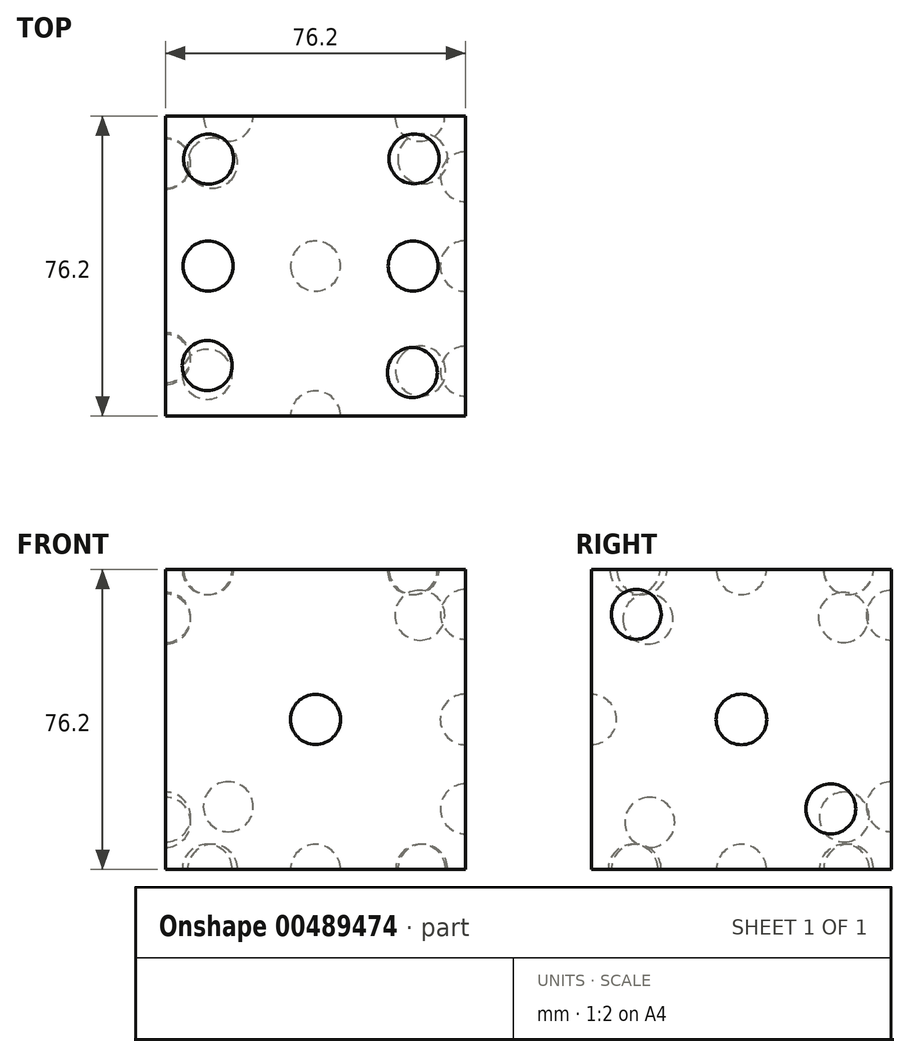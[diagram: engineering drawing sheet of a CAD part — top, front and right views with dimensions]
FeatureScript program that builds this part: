
annotation { "Feature Type Name" : "Feature", "Feature Type Description" : "" }
export const myFeature = defineFeature(function(context is Context, id is Id, definition is map)
    precondition{}
    {
        {
            var Q0;
            Q0=qCreatedBy(makeId("Front.planeOp"),FACE);
            var sketch = newSketch(context, id + "F0", { "sketchPlane" : qUnion([Q0])});
            skLineSegment(sketch, "E0", {"start": v(0, 0) * mm, "end": v(-76.2, 0) * mm});
            skLineSegment(sketch, "E1", {"start": v(0, 76.2) * mm, "end": v(-76.2, 76.2) * mm});
            skLineSegment(sketch, "E2", {"start": v(-76.2, 76.2) * mm, "end": v(-76.2, 0) * mm});
            skLineSegment(sketch, "E3", {"start": v(0, 76.2) * mm, "end": v(0, 0) * mm});
            skSolve(sketch);
        }
        {
            var Q0;
            Q0 = qSketchRegion(id + "F0", true);
            extrude(context, id + "F1", {"entities" : qUnion([Q0]), "depth" : 76.2 * mm});
        }
        {
            var Q0;
            Q0=makeQuery(id+"F1.opExtrude","CAP_FACE",FACE,{"disambiguationData":[OSD([sQuery(id+"F0.wireOp",EDGE,"E0"),sQuery(id+"F0.wireOp",EDGE,"E1"),sQuery(id+"F0.wireOp",EDGE,"E2"),sQuery(id+"F0.wireOp",EDGE,"E3")])],"isStart":false});
            var sketch = newSketch(context, id + "F2", { "sketchPlane" : qUnion([Q0])});
            skLineSegment(sketch, "E4", {"start": v(-38.1, 76.2) * mm, "end": v(-38.1, 0) * mm});
            skPoint(sketch, "E5.endSnap0", {"position": v(-76.2, 38.1) * mm});
            skPoint(sketch, "E6.end.orphan", {"position": v(0, 38.1) * mm});
            skPoint(sketch, "E7.orphan", {"position": v(-4, 38.1) * mm});
            skPoint(sketch, "E5.start.orphan", {"position": v(-76.2, 38.1) * mm});
            skArc(sketch, "E8", {"start": v(-38.1, 31.75) * mm, "mid": v(-31.75, 38.1) * mm, "end": v(-38.1, 44.45) * mm});
            skSolve(sketch);
        }
        {
            var Q0;
            Q0 = qSketchRegion(id + "F2", true);
            var Q1;
            Q1=sQuery(id+"F2.wireOp",EDGE,"E4");
            revolve(context, id + "F3", {"operationType" : NewBodyOperationType.REMOVE, "entities" : qUnion([Q0]), "axis" : qUnion([Q1]), "revolveType" : RevolveType.FULL, "oppositeDirection" : true});
        }
        {
            var Q0;
            Q0=makeQuery(id+"F1.opExtrude","CAP_FACE",FACE,{"disambiguationData":[OSD([sQuery(id+"F0.wireOp",EDGE,"E0"),sQuery(id+"F0.wireOp",EDGE,"E1"),sQuery(id+"F0.wireOp",EDGE,"E2"),sQuery(id+"F0.wireOp",EDGE,"E3")])],"isStart":true});
            var sketch = newSketch(context, id + "F4", { "sketchPlane" : qUnion([Q0])});
            skArc(sketch, "E9", {"start": v(11.38, 58.24) * mm, "mid": v(17.96, 64.61) * mm, "end": v(11.33, 70.93) * mm});
            skPoint(sketch, "E10.orphan", {"position": v(11.61, 0) * mm});
            skPoint(sketch, "E11.end.orphan", {"position": v(11.61, 76.2) * mm});
            skPoint(sketch, "E12.orphan", {"position": v(59.49, 0) * mm});
            skPoint(sketch, "E13.orphan", {"position": v(59.49, 76.2) * mm});
            skLineSegment(sketch, "E14", {"start": v(11.61, 76.2) * mm, "end": v(11.61, 0) * mm});
            skSolve(sketch);
        }
        {
            var Q0;
            Q0 = qSketchRegion(id + "F4", true);
            var Q1;
            Q1=sQuery(id+"F4.wireOp",EDGE,"E14");
            revolve(context, id + "F5", {"operationType" : NewBodyOperationType.REMOVE, "entities" : qUnion([Q0]), "axis" : qUnion([Q1]), "revolveType" : RevolveType.FULL, "oppositeDirection" : true});
        }
        {
            var Q0;
            Q0=makeQuery(id+"F1.opExtrude","CAP_FACE",FACE,{"disambiguationData":[OSD([sQuery(id+"F0.wireOp",EDGE,"E0"),sQuery(id+"F0.wireOp",EDGE,"E1"),sQuery(id+"F0.wireOp",EDGE,"E2"),sQuery(id+"F0.wireOp",EDGE,"E3")])],"isStart":true});
            var sketch = newSketch(context, id + "F6", { "sketchPlane" : qUnion([Q0])});
            skArc(sketch, "E15", {"start": v(60.26, 9.59) * mm, "mid": v(66.61, 15.94) * mm, "end": v(60.26, 22.29) * mm});
            skLineSegment(sketch, "E16", {"start": v(60.26, 76.2) * mm, "end": v(60.26, 0) * mm});
            skSolve(sketch);
        }
        {
            var Q0;
            Q0 = qSketchRegion(id + "F6", true);
            var Q1;
            Q1=sQuery(id+"F6.wireOp",EDGE,"E16");
            revolve(context, id + "F7", {"operationType" : NewBodyOperationType.REMOVE, "entities" : qUnion([Q0]), "axis" : qUnion([Q1]), "revolveType" : RevolveType.FULL, "oppositeDirection" : true});
        }
        {
            var Q0;
            Q0=makeQuery(id+"F1.opExtrude","SWEPT_FACE",FACE,{"disambiguationData":[OSD([sQuery(id+"F0.wireOp",EDGE,"E3")])]});
            var sketch = newSketch(context, id + "F8", { "sketchPlane" : qUnion([Q0])});
            skArc(sketch, "E17", {"start": v(-64.83, 58.48) * mm, "mid": v(-58.48, 64.83) * mm, "end": v(-64.83, 71.18) * mm});
            skPoint(sketch, "E18.orphan", {"position": v(-76.2, 76.2) * mm});
            skPoint(sketch, "E19.trimOffspring.end.orphan", {"position": v(0, 0) * mm});
            skLineSegment(sketch, "E20", {"start": v(-64.83, 76.2) * mm, "end": v(-64.83, 0) * mm});
            skPoint(sketch, "E21.orphan", {"position": v(-38.1, 76.2) * mm});
            skPoint(sketch, "E22.center.orphan", {"position": v(-38.1, 38.1) * mm});
            skPoint(sketch, "E23.end.orphan", {"position": v(-38.1, 0) * mm});
            skPoint(sketch, "E24.orphan", {"position": v(-12.52, 76.2) * mm});
            skPoint(sketch, "E25.center.orphan", {"position": v(-12.52, 12.52) * mm});
            skSolve(sketch);
        }
        {
            var Q0;
            Q0 = qSketchRegion(id + "F8", true);
            var Q1;
            Q1=sQuery(id+"F8.wireOp",EDGE,"E20");
            revolve(context, id + "F9", {"operationType" : NewBodyOperationType.REMOVE, "entities" : qUnion([Q0]), "axis" : qUnion([Q1]), "revolveType" : RevolveType.FULL, "oppositeDirection" : true});
        }
        {
            var Q0;
            Q0=makeQuery(id+"F1.opExtrude","SWEPT_FACE",FACE,{"disambiguationData":[OSD([sQuery(id+"F0.wireOp",EDGE,"E3")])]});
            var sketch = newSketch(context, id + "F10", { "sketchPlane" : qUnion([Q0])});
            skArc(sketch, "E26", {"start": v(-38.1, 31.67) * mm, "mid": v(-31.67, 38.1) * mm, "end": v(-38.1, 44.53) * mm});
            skPoint(sketch, "E27.orphan", {"position": v(-76.2, 76.2) * mm});
            skPoint(sketch, "E28.orphan", {"position": v(0, 0) * mm});
            skLineSegment(sketch, "E29", {"start": v(-38.1, 76.2) * mm, "end": v(-38.1, 0) * mm});
            skSolve(sketch);
        }
        {
            var Q0;
            Q0 = qSketchRegion(id + "F10", true);
            var Q1;
            Q1=sQuery(id+"F10.wireOp",EDGE,"E29");
            revolve(context, id + "F11", {"operationType" : NewBodyOperationType.REMOVE, "entities" : qUnion([Q0]), "axis" : qUnion([Q1]), "revolveType" : RevolveType.FULL, "oppositeDirection" : true});
        }
        {
            var Q0;
            Q0=makeQuery(id+"F1.opExtrude","SWEPT_FACE",FACE,{"disambiguationData":[OSD([sQuery(id+"F0.wireOp",EDGE,"E3")])]});
            var sketch = newSketch(context, id + "F12", { "sketchPlane" : qUnion([Q0])});
            skArc(sketch, "E30", {"start": v(-15.4, 9.05) * mm, "mid": v(-9.05, 15.4) * mm, "end": v(-15.4, 21.75) * mm});
            skLineSegment(sketch, "E31", {"start": v(-15.4, 76.2) * mm, "end": v(-15.4, 0) * mm});
            skSolve(sketch);
        }
        {
            var Q0;
            Q0 = qSketchRegion(id + "F12", true);
            var Q1;
            Q1=sQuery(id+"F12.wireOp",EDGE,"E31");
            revolve(context, id + "F13", {"operationType" : NewBodyOperationType.REMOVE, "entities" : qUnion([Q0]), "axis" : qUnion([Q1]), "revolveType" : RevolveType.FULL, "oppositeDirection" : true});
        }
        {
            var Q0;
            Q0=makeQuery(id+"F1.opExtrude","SWEPT_FACE",FACE,{"disambiguationData":[OSD([sQuery(id+"F0.wireOp",EDGE,"E2")])]});
            var sketch = newSketch(context, id + "F14", { "sketchPlane" : qUnion([Q0])});
            skArc(sketch, "E32", {"start": v(12.17, 57.68) * mm, "mid": v(18.52, 64.03) * mm, "end": v(12.17, 70.38) * mm});
            skLineSegment(sketch, "E33", {"start": v(12.17, 76.2) * mm, "end": v(12.17, 0) * mm});
            skSolve(sketch);
        }
        {
            var Q0;
            Q0 = qSketchRegion(id + "F14", true);
            var Q1;
            Q1=sQuery(id+"F14.wireOp",EDGE,"E33");
            revolve(context, id + "F15", {"operationType" : NewBodyOperationType.REMOVE, "entities" : qUnion([Q0]), "axis" : qUnion([Q1]), "revolveType" : RevolveType.FULL, "oppositeDirection" : true});
        }
        {
            var Q0;
            Q0=makeQuery(id+"F1.opExtrude","SWEPT_FACE",FACE,{"disambiguationData":[OSD([sQuery(id+"F0.wireOp",EDGE,"E2")])]});
            var sketch = newSketch(context, id + "F16", { "sketchPlane" : qUnion([Q0])});
            skLineSegment(sketch, "E34", {"start": v(11.97, 76.2) * mm, "end": v(11.97, 0) * mm});
            skArc(sketch, "E35", {"start": v(11.97, 6.95) * mm, "mid": v(18.32, 13.3) * mm, "end": v(11.97, 19.65) * mm});
            skSolve(sketch);
        }
        {
            var Q0;
            Q0 = qSketchRegion(id + "F16", true);
            var Q1;
            Q1=sQuery(id+"F16.wireOp",EDGE,"E34");
            revolve(context, id + "F17", {"operationType" : NewBodyOperationType.REMOVE, "entities" : qUnion([Q0]), "axis" : qUnion([Q1]), "revolveType" : RevolveType.FULL, "oppositeDirection" : true});
        }
        {
            var Q0;
            Q0=makeQuery(id+"F1.opExtrude","SWEPT_FACE",FACE,{"disambiguationData":[OSD([sQuery(id+"F0.wireOp",EDGE,"E2")])]});
            var sketch = newSketch(context, id + "F18", { "sketchPlane" : qUnion([Q0])});
            skLineSegment(sketch, "E36", {"start": v(0, 63.6) * mm, "end": v(76.2, 63.6) * mm});
            skArc(sketch, "E37", {"start": v(68.19, 63.6) * mm, "mid": v(61.84, 69.96) * mm, "end": v(55.49, 63.6) * mm});
            skSolve(sketch);
        }
        {
            var Q0;
            Q0 = qSketchRegion(id + "F18", true);
            var Q1;
            Q1=sQuery(id+"F18.wireOp",EDGE,"E36");
            revolve(context, id + "F19", {"operationType" : NewBodyOperationType.REMOVE, "entities" : qUnion([Q0]), "axis" : qUnion([Q1]), "revolveType" : RevolveType.FULL, "oppositeDirection" : true});
        }
        {
            var Q0;
            Q0=makeQuery(id+"F1.opExtrude","SWEPT_FACE",FACE,{"disambiguationData":[OSD([sQuery(id+"F0.wireOp",EDGE,"E2")])]});
            var sketch = newSketch(context, id + "F20", { "sketchPlane" : qUnion([Q0])});
            skLineSegment(sketch, "E38", {"start": v(61.4, 76.2) * mm, "end": v(61.4, 0) * mm});
            skArc(sketch, "E39", {"start": v(61.4, 5.62) * mm, "mid": v(67.74, 11.97) * mm, "end": v(61.4, 18.32) * mm});
            skSolve(sketch);
        }
        {
            var Q0;
            Q0 = qSketchRegion(id + "F20", true);
            var Q1;
            Q1=sQuery(id+"F20.wireOp",EDGE,"E38");
            revolve(context, id + "F21", {"operationType" : NewBodyOperationType.REMOVE, "entities" : qUnion([Q0]), "axis" : qUnion([Q1]), "revolveType" : RevolveType.FULL, "oppositeDirection" : true});
        }
        {
            var Q0;
            Q0=makeQuery(id+"F1.opExtrude","SWEPT_FACE",FACE,{"disambiguationData":[OSD([sQuery(id+"F0.wireOp",EDGE,"E0")])]});
            var sketch = newSketch(context, id + "F22", { "sketchPlane" : qUnion([Q0])});
            skLineSegment(sketch, "E40", {"start": v(-76.2, 76.2) * mm, "end": v(0, 0) * mm});
            skArc(sketch, "E41", {"start": v(-61.11, 61.11) * mm, "mid": v(-61.11, 70.1) * mm, "end": v(-70.1, 70.1) * mm});
            skSolve(sketch);
        }
        {
            var Q0;
            Q0 = qSketchRegion(id + "F22", true);
            var Q1;
            Q1=sQuery(id+"F22.wireOp",EDGE,"E40");
            revolve(context, id + "F23", {"operationType" : NewBodyOperationType.REMOVE, "entities" : qUnion([Q0]), "axis" : qUnion([Q1]), "revolveType" : RevolveType.FULL, "oppositeDirection" : true});
        }
        {
            var Q0;
            Q0=makeQuery(id+"F1.opExtrude","SWEPT_FACE",FACE,{"disambiguationData":[OSD([sQuery(id+"F0.wireOp",EDGE,"E0")])]});
            var sketch = newSketch(context, id + "F24", { "sketchPlane" : qUnion([Q0])});
            skLineSegment(sketch, "E42", {"start": v(-76.2, 76.2) * mm, "end": v(0, 0) * mm});
            skArc(sketch, "E43", {"start": v(-33.6, 33.6) * mm, "mid": v(-33.6, 42.6) * mm, "end": v(-42.6, 42.6) * mm});
            skSolve(sketch);
        }
        {
            var Q0;
            Q0 = qSketchRegion(id + "F24", true);
            var Q1;
            Q1=sQuery(id+"F24.wireOp",EDGE,"E42");
            revolve(context, id + "F25", {"operationType" : NewBodyOperationType.REMOVE, "entities" : qUnion([Q0]), "axis" : qUnion([Q1]), "revolveType" : RevolveType.FULL, "oppositeDirection" : true});
        }
        {
            var Q0;
            Q0=makeQuery(id+"F1.opExtrude","SWEPT_FACE",FACE,{"disambiguationData":[OSD([sQuery(id+"F0.wireOp",EDGE,"E0")])]});
            var sketch = newSketch(context, id + "F26", { "sketchPlane" : qUnion([Q0])});
            skLineSegment(sketch, "E44", {"start": v(-76.2, 76.2) * mm, "end": v(0, 0) * mm});
            skArc(sketch, "E45", {"start": v(-6.37, 6.37) * mm, "mid": v(-6.37, 15.35) * mm, "end": v(-15.35, 15.35) * mm});
            skSolve(sketch);
        }
        {
            var Q0;
            Q0 = qSketchRegion(id + "F26", true);
            var Q1;
            Q1=sQuery(id+"F26.wireOp",EDGE,"E44");
            revolve(context, id + "F27", {"operationType" : NewBodyOperationType.REMOVE, "entities" : qUnion([Q0]), "axis" : qUnion([Q1]), "revolveType" : RevolveType.FULL, "oppositeDirection" : true});
        }
        {
            var Q0;
            Q0=makeQuery(id+"F1.opExtrude","SWEPT_FACE",FACE,{"disambiguationData":[OSD([sQuery(id+"F0.wireOp",EDGE,"E0")])]});
            var sketch = newSketch(context, id + "F28", { "sketchPlane" : qUnion([Q0])});
            skLineSegment(sketch, "E46", {"start": v(0, 76.2) * mm, "end": v(-76.2, 0) * mm});
            skArc(sketch, "E47", {"start": v(-68.74, 7.46) * mm, "mid": v(-59.76, 7.46) * mm, "end": v(-59.76, 16.44) * mm});
            skSolve(sketch);
        }
        {
            var Q0;
            Q0 = qSketchRegion(id + "F28", true);
            var Q1;
            Q1=sQuery(id+"F28.wireOp",EDGE,"E46");
            revolve(context, id + "F29", {"operationType" : NewBodyOperationType.REMOVE, "entities" : qUnion([Q0]), "axis" : qUnion([Q1]), "revolveType" : RevolveType.FULL, "oppositeDirection" : true});
        }
        {
            var Q0;
            Q0=makeQuery(id+"F1.opExtrude","SWEPT_FACE",FACE,{"disambiguationData":[OSD([sQuery(id+"F0.wireOp",EDGE,"E0")])]});
            var sketch = newSketch(context, id + "F30", { "sketchPlane" : qUnion([Q0])});
            skLineSegment(sketch, "E48", {"start": v(0, 76.2) * mm, "end": v(-76.2, 0) * mm});
            skArc(sketch, "E49", {"start": v(-15.88, 60.32) * mm, "mid": v(-6.9, 60.32) * mm, "end": v(-6.9, 69.3) * mm});
            skSolve(sketch);
        }
        {
            var Q0;
            Q0 = qSketchRegion(id + "F30", true);
            var Q1;
            Q1=sQuery(id+"F30.wireOp",EDGE,"E48");
            revolve(context, id + "F31", {"operationType" : NewBodyOperationType.REMOVE, "entities" : qUnion([Q0]), "axis" : qUnion([Q1]), "revolveType" : RevolveType.FULL, "oppositeDirection" : true});
        }
        {
            var Q0;
            Q0=makeQuery(id+"F1.opExtrude","SWEPT_FACE",FACE,{"disambiguationData":[OSD([sQuery(id+"F0.wireOp",EDGE,"E1")])]});
            var sketch = newSketch(context, id + "F32", { "sketchPlane" : qUnion([Q0])});
            skLineSegment(sketch, "E50", {"start": v(-76.2, 0) * mm, "end": v(0, -76.2) * mm});
            skArc(sketch, "E51", {"start": v(-60.76, -15.44) * mm, "mid": v(-60.76, -6.46) * mm, "end": v(-69.74, -6.46) * mm});
            skSolve(sketch);
        }
        {
            var Q0;
            Q0 = qSketchRegion(id + "F32", true);
            var Q1;
            Q1=sQuery(id+"F32.wireOp",EDGE,"E50");
            revolve(context, id + "F33", {"operationType" : NewBodyOperationType.REMOVE, "entities" : qUnion([Q0]), "axis" : qUnion([Q1]), "revolveType" : RevolveType.FULL, "oppositeDirection" : true});
        }
        {
            var Q0;
            Q0=makeQuery(id+"F1.opExtrude","SWEPT_FACE",FACE,{"disambiguationData":[OSD([sQuery(id+"F0.wireOp",EDGE,"E1")])]});
            var sketch = newSketch(context, id + "F34", { "sketchPlane" : qUnion([Q0])});
            skLineSegment(sketch, "E52", {"start": v(-65.38, 0) * mm, "end": v(-65.38, -76.2) * mm});
            skArc(sketch, "E53", {"start": v(-65.38, -44.45) * mm, "mid": v(-59.03, -38.1) * mm, "end": v(-65.38, -31.75) * mm});
            skSolve(sketch);
        }
        {
            var Q0;
            Q0 = qSketchRegion(id + "F34", true);
            var Q1;
            Q1=sQuery(id+"F34.wireOp",EDGE,"E52");
            revolve(context, id + "F35", {"operationType" : NewBodyOperationType.REMOVE, "entities" : qUnion([Q0]), "axis" : qUnion([Q1]), "revolveType" : RevolveType.FULL, "oppositeDirection" : true});
        }
        {
            var Q0;
            Q0=makeQuery(id+"F1.opExtrude","SWEPT_FACE",FACE,{"disambiguationData":[OSD([sQuery(id+"F0.wireOp",EDGE,"E1")])]});
            var sketch = newSketch(context, id + "F36", { "sketchPlane" : qUnion([Q0])});
            skLineSegment(sketch, "E54", {"start": v(-65.6, -76.2) * mm, "end": v(-65.6, 0) * mm});
            skArc(sketch, "E55", {"start": v(-65.6, -69.74) * mm, "mid": v(-59.25, -63.39) * mm, "end": v(-65.6, -57.04) * mm});
            skSolve(sketch);
        }
        {
            var Q0;
            Q0 = qSketchRegion(id + "F36", true);
            var Q1;
            Q1=sQuery(id+"F36.wireOp",EDGE,"E54");
            revolve(context, id + "F37", {"operationType" : NewBodyOperationType.REMOVE, "entities" : qUnion([Q0]), "axis" : qUnion([Q1]), "revolveType" : RevolveType.FULL, "oppositeDirection" : true});
        }
        {
            var Q0;
            Q0=makeQuery(id+"F1.opExtrude","SWEPT_FACE",FACE,{"disambiguationData":[OSD([sQuery(id+"F0.wireOp",EDGE,"E1")])]});
            var sketch = newSketch(context, id + "F38", { "sketchPlane" : qUnion([Q0])});
            skLineSegment(sketch, "E56", {"start": v(-76.2, -10.86) * mm, "end": v(0, -10.86) * mm});
            skArc(sketch, "E57", {"start": v(-6.73, -10.86) * mm, "mid": v(-13.08, -4.51) * mm, "end": v(-19.43, -10.86) * mm});
            skSolve(sketch);
        }
        {
            var Q0;
            Q0 = qSketchRegion(id + "F38", true);
            var Q1;
            Q1=sQuery(id+"F38.wireOp",EDGE,"E56");
            revolve(context, id + "F39", {"operationType" : NewBodyOperationType.REMOVE, "entities" : qUnion([Q0]), "axis" : qUnion([Q1]), "revolveType" : RevolveType.FULL, "oppositeDirection" : true});
        }
        {
            var Q0;
            Q0=makeQuery(id+"F1.opExtrude","SWEPT_FACE",FACE,{"disambiguationData":[OSD([sQuery(id+"F0.wireOp",EDGE,"E1")])]});
            var sketch = newSketch(context, id + "F40", { "sketchPlane" : qUnion([Q0])});
            skLineSegment(sketch, "E58", {"start": v(-13.3, 0) * mm, "end": v(-13.3, -76.2) * mm});
            skArc(sketch, "E59", {"start": v(-13.3, -44.45) * mm, "mid": v(-6.95, -38.1) * mm, "end": v(-13.3, -31.75) * mm});
            skSolve(sketch);
        }
        {
            var Q0;
            Q0 = qSketchRegion(id + "F40", true);
            var Q1;
            Q1=sQuery(id+"F40.wireOp",EDGE,"E58");
            revolve(context, id + "F41", {"operationType" : NewBodyOperationType.REMOVE, "entities" : qUnion([Q0]), "axis" : qUnion([Q1]), "revolveType" : RevolveType.FULL, "oppositeDirection" : true});
        }
        {
            var Q0;
            Q0=makeQuery(id+"F1.opExtrude","SWEPT_FACE",FACE,{"disambiguationData":[OSD([sQuery(id+"F0.wireOp",EDGE,"E1")])]});
            var sketch = newSketch(context, id + "F42", { "sketchPlane" : qUnion([Q0])});
            skLineSegment(sketch, "E60", {"start": v(-13.52, 0) * mm, "end": v(-13.52, -76.2) * mm});
            skArc(sketch, "E61", {"start": v(-13.52, -71.51) * mm, "mid": v(-7.17, -65.16) * mm, "end": v(-13.52, -58.81) * mm});
            skSolve(sketch);
        }
        {
            var Q0;
            Q0 = qSketchRegion(id + "F42", true);
            var Q1;
            Q1=sQuery(id+"F42.wireOp",EDGE,"E60");
            revolve(context, id + "F43", {"operationType" : NewBodyOperationType.REMOVE, "entities" : qUnion([Q0]), "axis" : qUnion([Q1]), "revolveType" : RevolveType.FULL, "oppositeDirection" : true});
        }
    });
